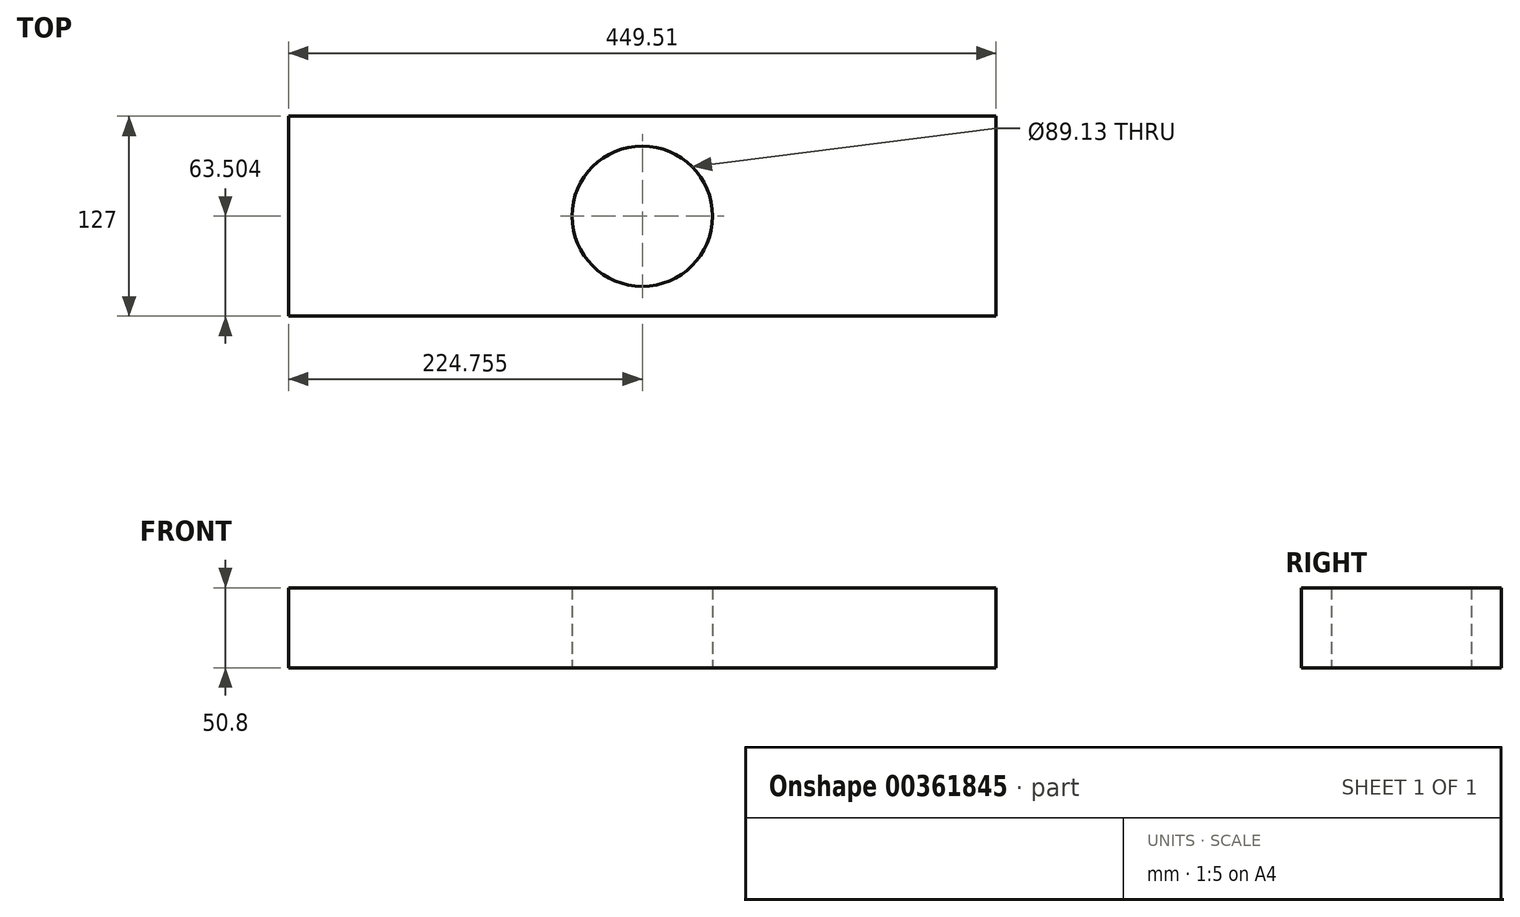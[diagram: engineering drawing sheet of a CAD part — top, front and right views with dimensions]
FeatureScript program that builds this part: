
annotation { "Feature Type Name" : "Feature", "Feature Type Description" : "" }
export const myFeature = defineFeature(function(context is Context, id is Id, definition is map)
    precondition{}
    {
        {
            var Q0;
            Q0=qCreatedBy(makeId("Top.planeOp"),FACE);
            var sketch = newSketch(context, id + "F0", { "sketchPlane" : qUnion([Q0])});
            skLineSegment(sketch, "E0.bottom", {"start": v(-201.12, 60) * mm, "end": v(248.39, 60) * mm});
            skLineSegment(sketch, "E0.top", {"start": v(-201.12, -67) * mm, "end": v(248.39, -67) * mm});
            skLineSegment(sketch, "E0.left", {"start": v(-201.12, 60) * mm, "end": v(-201.12, -67) * mm});
            skLineSegment(sketch, "E0.right", {"start": v(248.39, 60) * mm, "end": v(248.39, -67) * mm});
            skCircle(sketch, "E1", {"center": v(23.63, -3.5) * mm, "radius": 44.56 * mm});
            skSolve(sketch);
        }
        {
            var Q0;
            Q0=makeQuery(id+"F0.imprint","IMPRINT",FACE,{"disambiguationData":[TD([[makeQuery(id+"F0.imprint","IMPRINT",EDGE,{"derivedFrom":sQuery(id+"F0.wireOp",EDGE,"E0.bottom")}),-1.0]])]});
            extrude(context, id + "F1", {"entities" : qUnion([Q0]), "depth" : 50.8 * mm});
        }
        {
            var Q0;
            Q0=qSketchRegion(id+"F0",true);
            extrude(context, id + "F2", {"entities" : qUnion([Q0]), "operationType" : NewBodyOperationType.ADD, "depth" : 50.8 * mm});
        }
    });
